# Revit family: Projector-LCD-Panasonic-Ultra_Short_Distance-PT-CMZ50X
name_source: partatom
category: Communication Devices
units: mm (PartAtom-declared; Revit-internal decimal feet)

## family parameters
Cut with Voids When Loaded = Yes
Host = Face
Maintain Annotation Orientation = No
OmniClass Number = 23.85.10.17.11.21
OmniClass Title = Data/Multi/Media Projectors
Part Type = Normal
Room Calculation Point = No
Round Connector Dimension = Use Diameter
Shared = No

## types (1)
- PT-CMZ50
    524_mm = High_Ceiling_Height : 524_mm
    564_mm = High_Ceiling_Height : 564_mm
    604_mm = High_Ceiling_Height : 604_mm
    Audio In = M3 stereo mini-jack x1
    Brightness = 5200 lm
    Brightness Economy = 3640 lm
    Brightness Full = 5200 lm
    Chip Diagonal = 16.3 mm
    Chip Quantity = 1
    Contrast Ratio = 3000000
    DC Out = USB connector (Type A) x 1
    DIGITAL LINK = RJ-45 x 1
    Date Last Modified = 2023/03/24
    Default Elevation = 0 mm  [stored 0 ft]
    Depth = 421 mm  [stored 1.38123 ft]
    Description = 5,200 Lumens, 16:10 Aspect Ratio, Ultra Short Throw Projector PT-CMZ50
    Equipment Abbreviation = LVP
    Family Version = 1.0.0
    HDMI In = HDMI™ 19pin x 1
    Heat Load Active = 1110.00 Btu/h
    Height = 176 mm
    LAN = RJ-45 x 1
    Lamp Life Economy = 24000
    Lamp Life Full = 20000
    Lamp Quantity = 1
    Lamp Type = Laser diode
    Lens Type = Fixed zoom, powered focus lens
    Manufacturer = Panasonic Connect Co., Ltd.
    Market = Commercial
    Model = PT-CMZ50
    Model Disclaimer = Contact Panasonic for more information
    Motorized Zoom = No
    Noise in High Mode = 34
    Noise in Low Mode = 25
    Part Description = 5,200 Lumens, 16:10 Aspect Ratio, Ultra Short Throw Projector PT-CMZ50
    Part Number = PT-CMZ50
    Power Active = 325 W
    Power Standby Eco = 1 W
    Power Standby Normal = 18 W
    Product Documentation Link = https://bizpartner.panasonic.net
    Product Material = Plastic - Panasonic - White
    Product Page URL = https://panasonic.net
    Provide Feedback = https://www.surveymonkey.com
    RGB In = D-sub 9-pin (female) x 1
    Resolution Horizontal = 1920
    Resolution Vertical = 1200
    Serial In = D-sub 9-pin (female) x 1
    Technology = Transparent LCD panel (x 3, R/G/B)
    Temperature Max = 113 °F
    Temperature Min = 32 °F
    Total Rated Watts = 325 W
    URL = http://panasonic.net
    USB = USB connector (Type A) x 1
    Variable Audio Out = M3 stereo mini-jack x 1
    WM_FB_Max = 665 mm
    WM_FB_Min = 395 mm
    WM_LR_Max = 41 mm
    WM_LR_Min = -49 mm  [stored -0.160761 ft]
    WM_UD_Max = 417 mm
    WM_UD_Min = 367 mm
    Weight = 20.15 lb
    Width = 495 mm  [stored 1.62402 ft]

note: [stored X ft] marks values corroborated as IEEE doubles in the binary element streams (Revit-internal decimal feet)

## geometry (parser evidence)
native form markers: Blend x8, Sweep x10
no freeform markers — native parametric forms only
